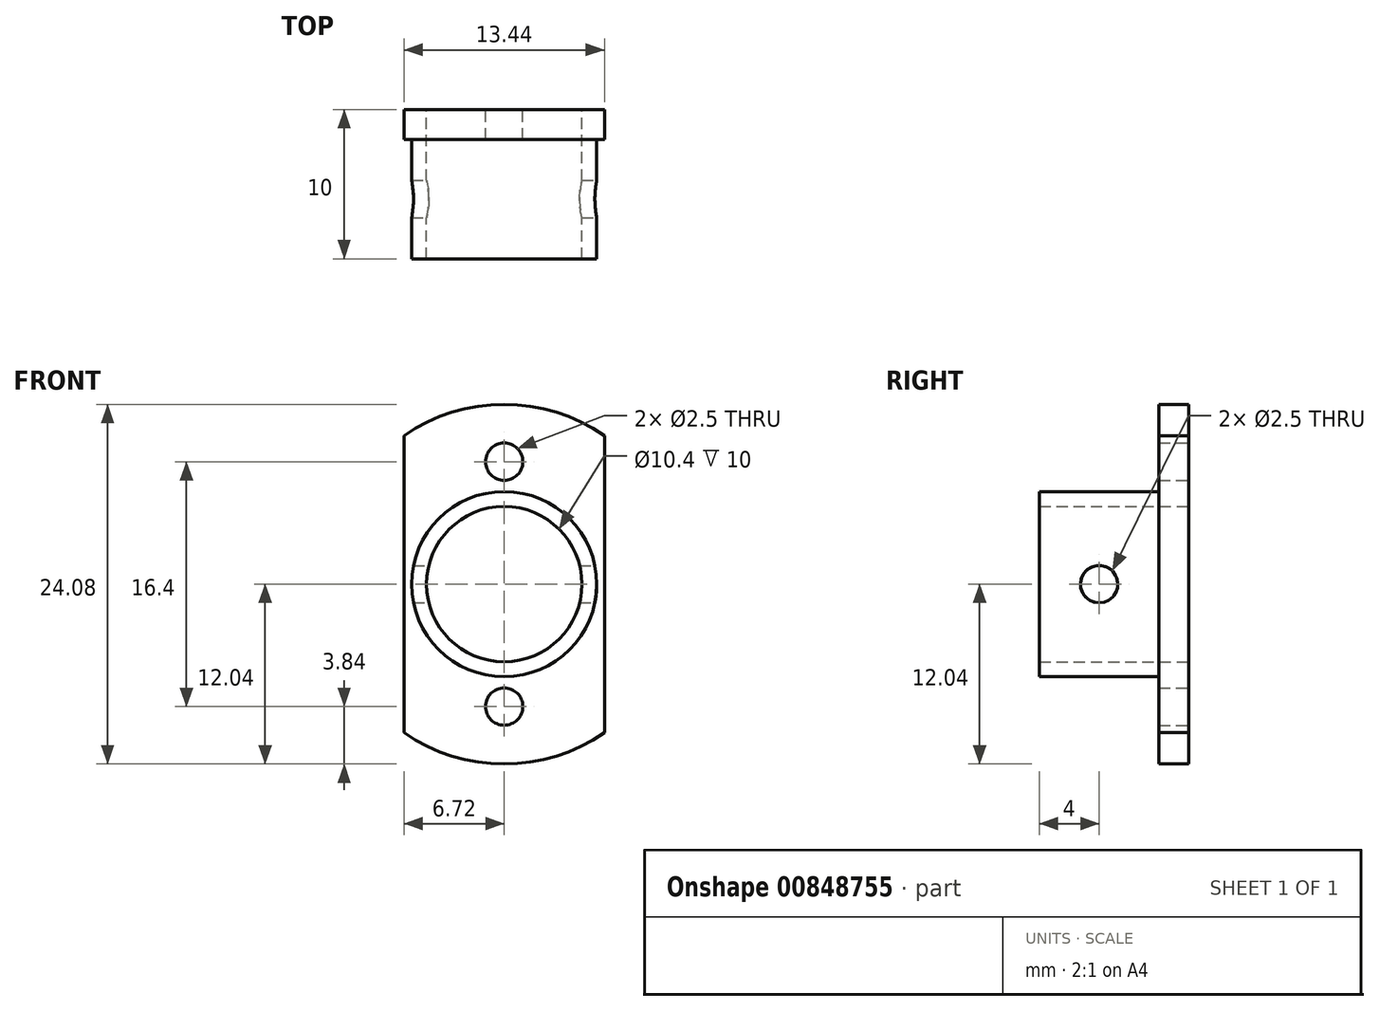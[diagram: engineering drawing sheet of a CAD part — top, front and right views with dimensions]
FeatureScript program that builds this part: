
annotation { "Feature Type Name" : "Feature", "Feature Type Description" : "" }
export const myFeature = defineFeature(function(context is Context, id is Id, definition is map)
    precondition{}
    {
        {
            var Q0;
            Q0=qCreatedBy(makeId("Front.planeOp"),FACE);
            var sketch = newSketch(context, id + "F0", { "sketchPlane" : qUnion([Q0])});
            skCircle(sketch, "E0", {"center": v(0, 0) * mm, "radius": 5.2 * mm});
            skLineSegment(sketch, "E1.top", {"start": v(8.72, -8.21) * mm, "end": v(-8.72, -8.21) * mm});
            skLineSegment(sketch, "E1.left", {"start": v(8.72, 8.21) * mm, "end": v(8.72, -8.21) * mm});
            skLineSegment(sketch, "E1.right", {"start": v(-8.72, 8.21) * mm, "end": v(-8.72, -8.21) * mm});
            skLineSegment(sketch, "E2", {"start": v(8.72, 8.21) * mm, "end": v(-8.72, 8.21) * mm});
            skPoint(sketch, "E3.snap10", {"position": v(0, -8.21) * mm});
            skArc(sketch, "E4", {"start": v(8.72, 8.21) * mm, "mid": v(0, 12.04) * mm, "end": v(-8.72, 8.21) * mm});
            skArc(sketch, "E5", {"start": v(-8.72, -8.21) * mm, "mid": v(0, -12.04) * mm, "end": v(8.72, -8.21) * mm});
            skLineSegment(sketch, "E6", {"start": v(-6.72, -9.95) * mm, "end": v(-6.72, 9.95) * mm});
            skLineSegment(sketch, "E7", {"start": v(6.72, -9.95) * mm, "end": v(6.72, 9.95) * mm});
            skCircle(sketch, "E8", {"center": v(0, 0) * mm, "radius": 6.2 * mm});
            skCircle(sketch, "E9", {"center": v(0, -8.2) * mm, "radius": 1.25 * mm});
            skCircle(sketch, "E10", {"center": v(0, 8.2) * mm, "radius": 1.25 * mm});
            skSolve(sketch);
        }
        {
            var Q0;
            Q0=makeQuery(id+"F0.imprint","IMPRINT",FACE,{"disambiguationData":[TD([[makeQuery(id+"F0.imprint","IMPRINT",EDGE,{"derivedFrom":sQuery(id+"F0.wireOp",EDGE,"E8")}),-1.0]])]});
            var Q1;
            {var subQ0=sQuery(id+"F0.wireOp",EDGE,"E7");var subQ1=sQuery(id+"F0.wireOp",EDGE,"E2");var subQ2=makeQuery(id+"F0.imprint","INTERSECT",VERTEX,{"derivedFrom":[subQ1,subQ0]});Q1=makeQuery(id+"F0.imprint","IMPRINT",FACE,{"disambiguationData":[TD([[makeQuery(id+"F0.imprint","IMPRINT",EDGE,{"disambiguationData":[TD([[subQ2,-1.0]])],"derivedFrom":subQ1}),-1.0]])]});}
            var Q2;
            {var subQ0=sQuery(id+"F0.wireOp",EDGE,"E7");var subQ1=sQuery(id+"F0.wireOp",EDGE,"E1.top");var subQ2=makeQuery(id+"F0.imprint","INTERSECT",VERTEX,{"derivedFrom":[subQ1,subQ0]});Q2=makeQuery(id+"F0.imprint","IMPRINT",FACE,{"disambiguationData":[TD([[makeQuery(id+"F0.imprint","IMPRINT",EDGE,{"disambiguationData":[TD([[subQ2,-1.0]])],"derivedFrom":subQ1}),1.0]])]});}
            extrude(context, id + "F1", {"entities" : qUnion([Q0, Q1, Q2]), "depth" : 2 * mm, "offsetDistance" : 25 * mm});
        }
        {
            var Q0;
            Q0=makeQuery(id+"F0.imprint","IMPRINT",FACE,{"disambiguationData":[TD([[makeQuery(id+"F0.imprint","IMPRINT",EDGE,{"derivedFrom":sQuery(id+"F0.wireOp",EDGE,"E0")}),-1.0]])]});
            extrude(context, id + "F2", {"entities" : qUnion([Q0]), "operationType" : NewBodyOperationType.ADD, "depth" : 10 * mm, "offsetDistance" : 25 * mm});
        }
        {
            var Q0;
            Q0=makeQuery(id+"F1.opExtrude","SWEPT_FACE",FACE,{"disambiguationData":[OSD([sQuery(id+"F0.wireOp",EDGE,"E7")])]});
            var sketch = newSketch(context, id + "F3", { "sketchPlane" : qUnion([Q0])});
            skCircle(sketch, "E11", {"center": v(-6, 0) * mm, "radius": 1.25 * mm});
            skSolve(sketch);
        }
        {
            var Q0;
            Q0=makeQuery(id+"F3.imprint","IMPRINT",FACE,{"disambiguationData":[TD([[makeQuery(id+"F3.imprint","IMPRINT",EDGE,{"derivedFrom":sQuery(id+"F3.wireOp",EDGE,"E11")}),1.0]])]});
            extrude(context, id + "F4", {"entities" : qUnion([Q0]), "operationType" : NewBodyOperationType.REMOVE, "oppositeDirection" : true, "depth" : 15 * mm, "offsetDistance" : 25 * mm});
        }
    });
